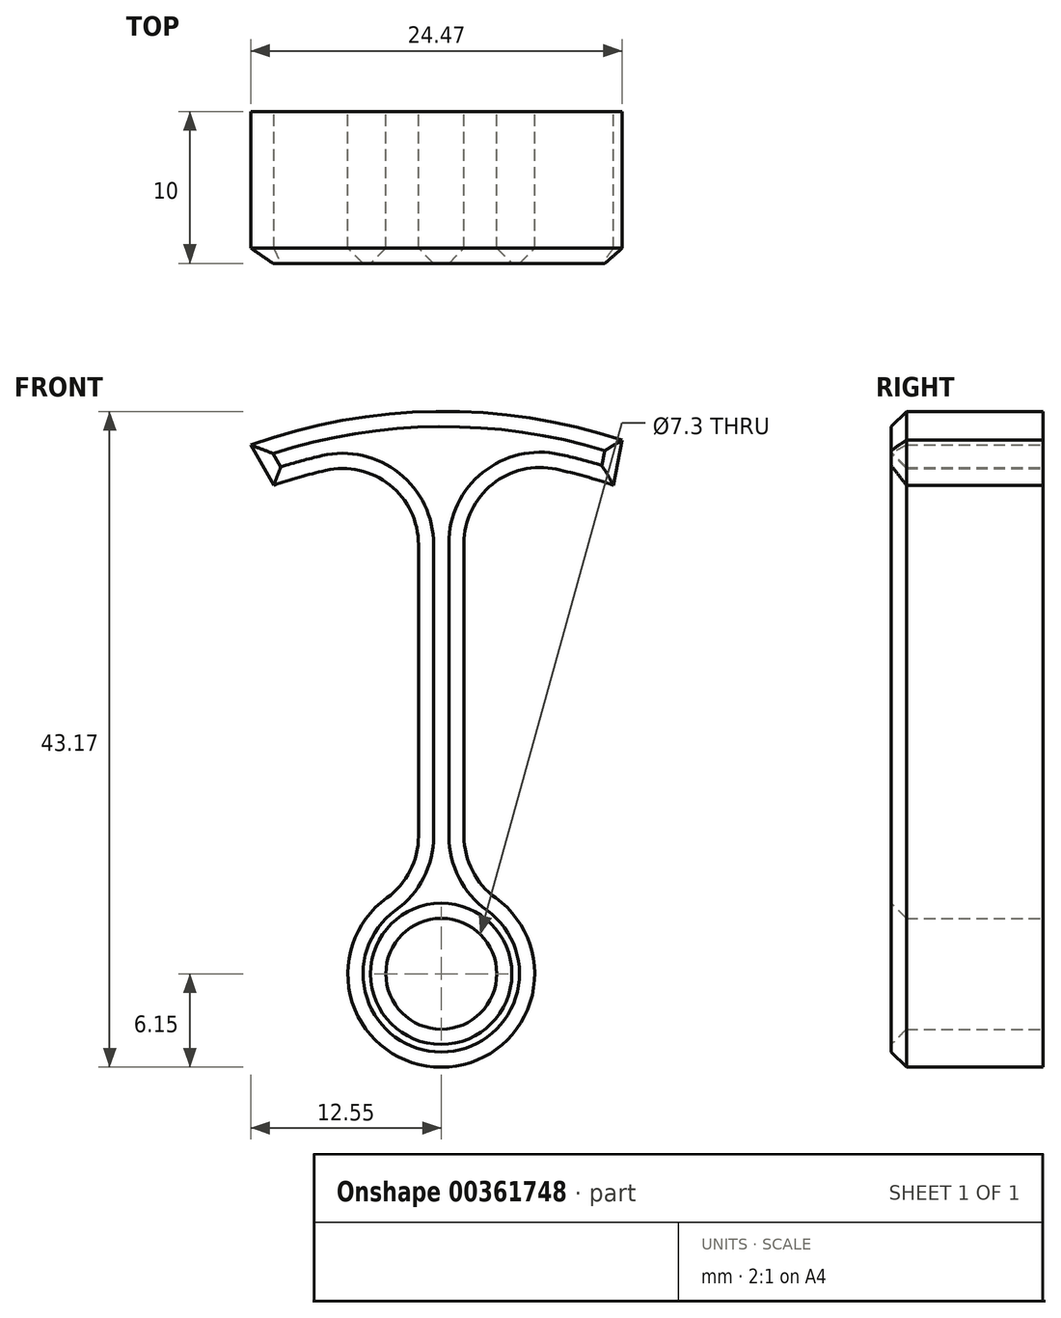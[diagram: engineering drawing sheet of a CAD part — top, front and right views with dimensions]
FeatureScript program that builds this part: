
annotation { "Feature Type Name" : "Feature", "Feature Type Description" : "" }
export const myFeature = defineFeature(function(context is Context, id is Id, definition is map)
    precondition{}
    {
        {
            var Q0;
            Q0=qCreatedBy(makeId("Front.planeOp"),FACE);
            var sketch = newSketch(context, id + "F0", { "sketchPlane" : qUnion([Q0])});
            skCircle(sketch, "E0", {"center": v(0, 0) * mm, "radius": 3.65 * mm});
            skArc(sketch, "E1.0", {"start": v(-1.5, 5.96) * mm, "mid": v(0, -6.15) * mm, "end": v(1.5, 5.96) * mm});
            skLineSegment(sketch, "E2", {"start": v(-1.5, 5.96) * mm, "end": v(-1.5, 32) * mm});
            skLineSegment(sketch, "E3", {"start": v(1.5, 5.96) * mm, "end": v(1.5, 32) * mm});
            skArc(sketch, "E4", {"start": v(11.92, 35.13) * mm, "mid": v(-0.34, 37.02) * mm, "end": v(-12.55, 34.8) * mm});
            skArc(sketch, "E5", {"start": v(11.35, 32.16) * mm, "mid": v(6.5, 33.44) * mm, "end": v(1.5, 34) * mm});
            skLineSegment(sketch, "E6", {"start": v(-1.5, 32) * mm, "end": v(-1.5, 33.98) * mm});
            skLineSegment(sketch, "E7", {"start": v(1.5, 32) * mm, "end": v(1.5, 34) * mm});
            skLineSegment(sketch, "E8.trimOffspring", {"start": v(-11.03, 32.16) * mm, "end": v(-12.55, 34.8) * mm});
            skLineSegment(sketch, "E9.trimOffspring", {"start": v(11.35, 32.16) * mm, "end": v(11.92, 35.13) * mm});
            skArc(sketch, "E10.trimOffspring", {"start": v(-1.5, 33.98) * mm, "mid": v(-6.33, 33.4) * mm, "end": v(-11.03, 32.16) * mm});
            skSolve(sketch);
        }
        {
            var Q0;
            Q0=makeQuery(id+"F0.imprint","IMPRINT",FACE,{"disambiguationData":[TD([[makeQuery(id+"F0.imprint","IMPRINT",EDGE,{"derivedFrom":sQuery(id+"F0.wireOp",EDGE,"E0")}),-1.0]])]});
            extrude(context, id + "F1", {"entities" : qUnion([Q0]), "depth" : 10 * mm, "offsetDistance" : 25 * mm});
        }
        {
            var Q0;
            Q0=makeQuery(id+"F1.opExtrude","SWEPT_EDGE",EDGE,{"disambiguationData":[OSD([sQuery(id+"F0.wireOp",EDGE,"E5"),sQuery(id+"F0.wireOp",EDGE,"E7")])]});
            var Q1;
            Q1=makeQuery(id+"F1.opExtrude","SWEPT_EDGE",EDGE,{"disambiguationData":[OSD([sQuery(id+"F0.wireOp",EDGE,"E6"),sQuery(id+"F0.wireOp",EDGE,"E10.trimOffspring")])]});
            var Q2;
            Q2=makeQuery(id+"F1.opExtrude","SWEPT_EDGE",EDGE,{"disambiguationData":[OSD([sQuery(id+"F0.wireOp",EDGE,"E1.0"),sQuery(id+"F0.wireOp",EDGE,"E3")])]});
            var Q3;
            Q3=makeQuery(id+"F1.opExtrude","SWEPT_EDGE",EDGE,{"disambiguationData":[OSD([sQuery(id+"F0.wireOp",EDGE,"E1.0"),sQuery(id+"F0.wireOp",EDGE,"E2")])]});
            fillet(context, id + "F2", {"entities" : qUnion([Q0, Q1, Q2, Q3]), "radius" : 5 * mm, "tangentPropagation" : true, "allowEdgeOverflow" : false});
        }
        {
            var Q0;
            Q0=makeQuery(id+"F1.opExtrude","CAP_FACE",FACE,{"disambiguationData":[OSD([sQuery(id+"F0.wireOp",EDGE,"E0"),sQuery(id+"F0.wireOp",EDGE,"E1.0"),sQuery(id+"F0.wireOp",EDGE,"E2"),sQuery(id+"F0.wireOp",EDGE,"E3"),sQuery(id+"F0.wireOp",EDGE,"E4"),sQuery(id+"F0.wireOp",EDGE,"E5"),sQuery(id+"F0.wireOp",EDGE,"E6"),sQuery(id+"F0.wireOp",EDGE,"E7"),sQuery(id+"F0.wireOp",EDGE,"E8.trimOffspring"),sQuery(id+"F0.wireOp",EDGE,"E9.trimOffspring"),sQuery(id+"F0.wireOp",EDGE,"E10.trimOffspring")])],"isStart":false});
            chamfer(context, id + "F3", {"entities" : qUnion([Q0]), "width" : 1 * mm, "tangentPropagation" : true});
        }
    });
